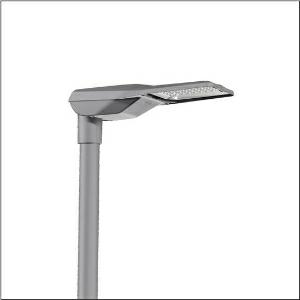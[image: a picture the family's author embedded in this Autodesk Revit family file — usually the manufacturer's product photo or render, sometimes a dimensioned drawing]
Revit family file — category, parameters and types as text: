
# Revit family: streetlight_sl_21_iq_mini___st0_8a_5xe2c31g08gb_0650
name_source: partatom
category: Lighting Fixtures
units: mm (PartAtom-declared; Revit-internal decimal feet)

## family parameters
Cut with Voids When Loaded = No
Host = Face
Light Source = No
Part Type = Normal
Room Calculation Point = No
Round Connector Dimension = Use Diameter
Shared = No

## types (1)
- --- (1 x LED, 5680 lm, 37.1 W, 3000K)
    Apparent Load = 37 VA
    CIE Flux Codes = 38 75 97 100 100
    Color Rendering = 70
    Color Temperature = 3000K
    Default Elevation = 1800 mm
    Description = Streetlight SL 21 mini, mast luminaire, primary light control with lens, of PMMA, primary optical cover: cover, of toughened safety glass, transparent, light distribution: ST0.8a, light emission: direct distribution, primary light characteristic: asymmetric, installation type: post-top, side-entry, LED, High Power LED, rated luminous flux: 5.680lm, luminous efficacy: 153lm/W, light colour: 730, colour temperature: 3000K, control gear: ECG iQ, control: Street-Remote, Auto-Match, Temp-Guard, Lumen-Switch, Night-Set, Smart-Wire, Light-Fading, Desk-Remote (wireless, voltage-free reading and setting of iQ features in the workshop via application-optimized NFC function/RFID function), optimised constant luminous flux control (CLO 2.0), mains connection: 220..240V, AC, 50/60Hz, start of lifetime: 37W, end of lifetime: 39W, reduction: 18W, luminaire housing, of diecast aluminium, powder-coated, Siteco® metallic grey (DB 702S), corrosivity category C5 according to DIN EN ISO 12944, length: 628mm, width: 235mm, height: 110mm, spigot size: 60/76mm (post-top) and 42/60/76mm (side-entry), mast flange for spigot size: 42mm: 5XC10008XM4, 60mm: 5XC10008XM2, 76/60mm: 5XC10108XM1, protection rating (complete): IP66, insulation class (complete): insulation class II (safety insulation), certification: CE, ENEC, VDE, impact resistance: IK09, permissible operating ambient temperature for outdoor applications: -40..+50°C, standard-compliant lighting for roads and squares, packaging unit: 1 piece

Light Distribution: ST0.8a
    Height = 110 mm
    Lamp = 1 x LED
    Lamp Light Flux = 5680 lm
    Lamp Power = 37.1 W
    Lamp count = 1
    Length = 625 mm
    Luminous efficacy = 153 lm/W
    Manufacturer = Siteco
    ModVariant = No
    Model = 5XE2C31G08GB
    Number of Poles = 1
    OnlyDefault = Yes
    Power Factor = 1
    Product Name = Streetlight SL 21 iQ mini | ST0.8a
    Product group = mast luminaire | pylon top
    ProductGroupID = 6100
    Protection Class = Protection class II
    Protection Degree = IP 66
    RLX_Detail_Level = 1
    RlxData = <blob elided: 91933 chars, md5=453f1051>
    Socket = socket
    Standby Power = 0 W
    System Light Flux = 5680 lm
    System Power = 37 W
    Type Comments = factory setting: luminous flux: 100 % | dim-lin: 254 | 385 mA
    Type Image = l_1003519.jpg
    URL = http://relux.com
    VarID = @adj_101923
    Voltage = 0 V
    Weight = 0.00 kg
    Width = 234 mm

## geometry (parser evidence)
native form markers: Blend x4, Sweep x10
no freeform markers — native parametric forms only
